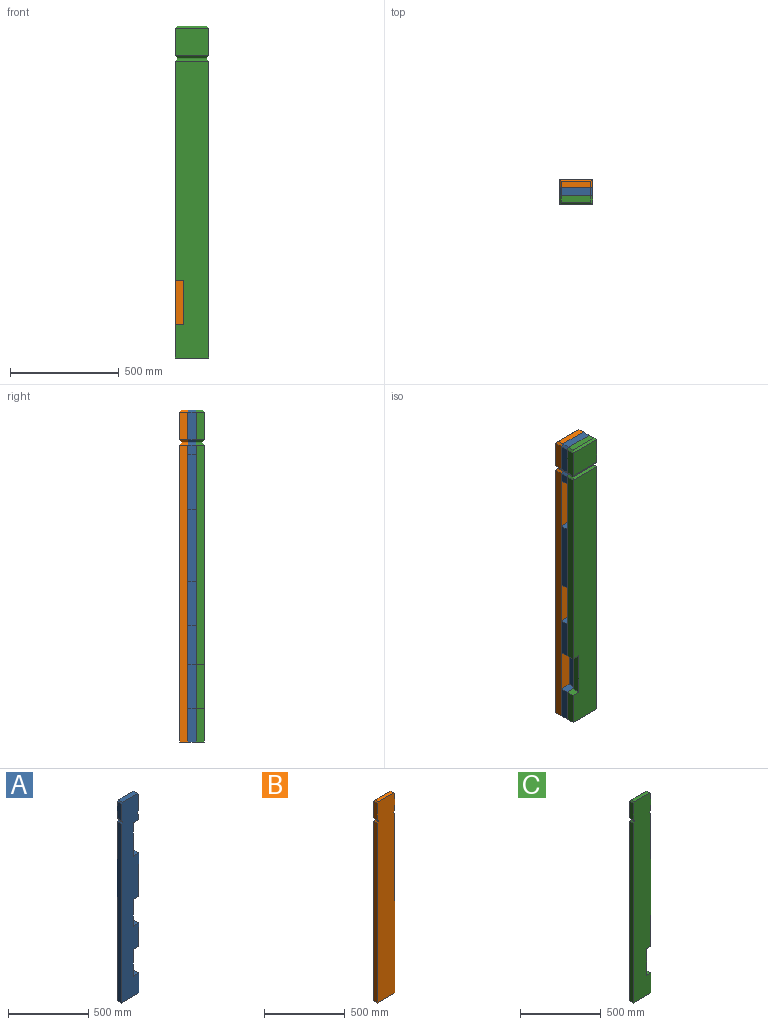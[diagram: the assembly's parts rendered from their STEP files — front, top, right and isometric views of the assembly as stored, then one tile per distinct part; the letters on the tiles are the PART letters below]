
ASSEMBLY  parts=3 mates=2
PART A: 28 faces, bbox 152.4x38.1x1524 mm
  f0: plane 177.8x38.1mm, normal (1,0,0), area 6774.2mm2, adj f4,f5,f13,f25
  f1: plane 127x38.1mm, normal (1,0,0), area 4838.7mm2, adj f4,f5,f20,f23
  f2: plane 127x38.1mm, normal (-1,0,0), area 4838.7mm2, adj f4,f5,f17,f24
  f3: plane 133.35x38.1mm, normal (0,0,1), area 5080.6mm2, adj f4,f5,f23,f24
  f4: plane 1524x152.4mm, normal (0,-1,0), area 198316.1mm2, adj f0,f1,f2,f3,f6,f7,f8,f9
  f5: plane 1524x152.4mm, normal (0,1,0), area 198316.1mm2, adj f0,f1,f2,f3,f6,f7,f8,f9
  f6: plane 41.28x38.1mm, normal (1,0,0), area 1572.6mm2, adj f4,f5,f14,f22
  f7: plane 330.2x38.1mm, normal (1,0,0), area 12580.6mm2, adj f4,f5,f11,f16
  f8: plane 1362.08x38.1mm, normal (-1,0,0), area 51895.1mm2, adj f4,f5,f9,f18
  f9: plane 152.4x38.1mm, normal (0,0,-1), area 5806.4mm2, adj f4,f5,f8,f10
  f10: plane 152.4x38.1mm, normal (1,0,0), area 5806.4mm2, adj f4,f5,f9,f27
  f11: plane 50.8x38.1mm, normal (0,0,-1), area 1935.5mm2, adj f4,f5,f7,f12
  f12: plane 203.2x38.1mm, normal (1,0,0), area 7741.9mm2, adj f4,f5,f11,f13
  f13: plane 50.8x38.1mm, normal (0,0,1), area 1935.5mm2, adj f0,f4,f5,f12
  f14: plane 50.8x38.1mm, normal (0,0,-1), area 1935.5mm2, adj f4,f5,f6,f15
  f15: plane 254x38.1mm, normal (1,0,0), area 9677.4mm2, adj f4,f5,f14,f16
  f16: plane 50.8x38.1mm, normal (0,0,1), area 1935.5mm2, adj f4,f5,f7,f15
  f17: plane 38.1x9.53mm, normal (-0.71,0,-0.71), area 513.2mm2, adj f2,f4,f5,f19
  f18: plane 38.1x9.53mm, normal (-0.71,0,0.71), area 513.2mm2, adj f4,f5,f8,f19
  f19: plane 38.1x6.35mm, normal (-1,0,0), area 241.9mm2, adj f4,f5,f17,f18
  f20: plane 38.1x9.53mm, normal (0.71,0,-0.71), area 513.2mm2, adj f1,f4,f5,f21
  f21: plane 38.1x6.35mm, normal (1,0,0), area 241.9mm2, adj f4,f5,f20,f22
  f22: plane 38.1x9.53mm, normal (0.71,0,0.71), area 513.2mm2, adj f4,f5,f6,f21
  f23: plane 38.1x9.53mm, normal (0.71,0,0.71), area 513.2mm2, adj f1,f3,f4,f5
  f24: plane 38.1x9.53mm, normal (-0.71,0,0.71), area 513.2mm2, adj f2,f3,f4,f5
  f25: plane 50.8x38.1mm, normal (0,0,-1), area 1935.5mm2, adj f0,f4,f5,f26
  f26: plane 203.2x38.1mm, normal (1,0,0), area 7741.9mm2, adj f4,f5,f25,f27
  f27: plane 50.8x38.1mm, normal (0,0,1), area 1935.5mm2, adj f4,f5,f10,f26
PART B: 21 faces, bbox 152.4x38.1x1524 mm
  f0: plane 152.4x127mm, normal (0,1,0), area 19354.8mm2, adj f3,f4,f17,f18
  f1: plane 38.1x9.53mm, normal (0.71,0,0.71), area 449.1mm2, adj f4,f5,f6,f17
  f2: plane 38.1x9.53mm, normal (-0.71,0,0.71), area 449.1mm2, adj f3,f5,f6,f17
  f3: plane 127x38.1mm, normal (-1,0,0), area 4838.7mm2, adj f0,f2,f6,f11
  f4: plane 127x38.1mm, normal (1,0,0), area 4838.7mm2, adj f0,f1,f6,f14
  f5: plane 133.35x28.58mm, normal (0,0,1), area 3810.5mm2, adj f1,f2,f6,f17
  f6: plane 1524x152.4mm, normal (0,-1,0), area 231864.5mm2, adj f1,f2,f3,f4,f5,f8,f9,f10
  f7: plane 1362.08x152.4mm, normal (0,1,0), area 207580.2mm2, adj f8,f9,f10,f20
  f8: plane 1362.08x38.1mm, normal (-1,0,0), area 51895.1mm2, adj f6,f7,f9,f12
  f9: plane 152.4x38.1mm, normal (0,0,-1), area 5806.4mm2, adj f6,f7,f8,f10
  f10: plane 1362.08x38.1mm, normal (1,0,0), area 51895.1mm2, adj f6,f7,f9,f16
  f11: plane 38.1x9.53mm, normal (-0.71,0,-0.71), area 449.1mm2, adj f3,f6,f13,f18
  f12: plane 38.1x9.53mm, normal (-0.71,0,0.71), area 449.1mm2, adj f6,f8,f13,f20
  f13: plane 28.58x6.35mm, normal (-1,0,0), area 181.5mm2, adj f6,f11,f12,f19
  f14: plane 38.1x9.53mm, normal (0.71,0,-0.71), area 449.1mm2, adj f4,f6,f15,f18
  f15: plane 28.58x6.35mm, normal (1,0,0), area 181.5mm2, adj f6,f14,f16,f19
  f16: plane 38.1x9.53mm, normal (0.71,0,0.71), area 449.1mm2, adj f6,f10,f15,f20
  f17: plane 152.4x9.53mm, normal (0,0.71,0.71), area 1924.6mm2, adj f0,f1,f2,f5
  f18: plane 152.4x9.53mm, normal (0,0.71,-0.71), area 1924.6mm2, adj f0,f11,f14,f19
  f19: plane 133.35x6.35mm, normal (0,1,0), area 846.8mm2, adj f13,f15,f18,f20
  f20: plane 152.4x9.53mm, normal (0,0.71,0.71), area 1924.6mm2, adj f7,f12,f16,f19
PART C: 25 faces, bbox 152.4x38.1x1524 mm
  f0: plane 152.4x127mm, normal (0,1,0), area 19354.8mm2, adj f4,f5,f21,f22
  f1: plane 38.1x9.53mm, normal (0.71,0,0.71), area 449.1mm2, adj f5,f6,f7,f21
  f2: plane 38.1x9.53mm, normal (-0.71,0,0.71), area 449.1mm2, adj f4,f6,f7,f21
  f3: plane 1006.48x38.1mm, normal (1,0,0), area 38346.7mm2, adj f7,f8,f17,f18
  f4: plane 127x38.1mm, normal (-1,0,0), area 4838.7mm2, adj f0,f2,f7,f12
  f5: plane 127x38.1mm, normal (1,0,0), area 4838.7mm2, adj f0,f1,f7,f15
  f6: plane 133.35x28.58mm, normal (0,0,1), area 3810.5mm2, adj f1,f2,f7,f21
  f7: plane 1524x152.4mm, normal (0,-1,0), area 224122.5mm2, adj f1,f2,f3,f4,f5,f6,f9,f10
  f8: plane 1362.08x152.4mm, normal (0,1,0), area 199838.3mm2, adj f3,f9,f10,f11,f18,f19,f20,f24
  f9: plane 1362.08x38.1mm, normal (-1,0,0), area 51895.1mm2, adj f7,f8,f10,f13
  f10: plane 152.4x38.1mm, normal (0,0,-1), area 5806.4mm2, adj f7,f8,f9,f11
  f11: plane 152.4x38.1mm, normal (1,0,0), area 5806.4mm2, adj f7,f8,f10,f20
  f12: plane 38.1x9.53mm, normal (-0.71,0,-0.71), area 449.1mm2, adj f4,f7,f14,f22
  f13: plane 38.1x9.53mm, normal (-0.71,0,0.71), area 449.1mm2, adj f7,f9,f14,f24
  f14: plane 28.58x6.35mm, normal (-1,0,0), area 181.5mm2, adj f7,f12,f13,f23
  f15: plane 38.1x9.53mm, normal (0.71,0,-0.71), area 449.1mm2, adj f5,f7,f16,f22
  f16: plane 28.58x6.35mm, normal (1,0,0), area 181.5mm2, adj f7,f15,f17,f23
  f17: plane 38.1x9.53mm, normal (0.71,0,0.71), area 449.1mm2, adj f3,f7,f16,f24
  f18: plane 38.1x38.1mm, normal (0,0,-1), area 1451.6mm2, adj f3,f7,f8,f19
  f19: plane 203.2x38.1mm, normal (1,0,0), area 7741.9mm2, adj f7,f8,f18,f20
  f20: plane 38.1x38.1mm, normal (0,0,1), area 1451.6mm2, adj f7,f8,f11,f19
  f21: plane 152.4x9.53mm, normal (0,0.71,0.71), area 1924.6mm2, adj f0,f1,f2,f6
  f22: plane 152.4x9.53mm, normal (0,0.71,-0.71), area 1924.6mm2, adj f0,f12,f15,f23
  f23: plane 133.35x6.35mm, normal (0,1,0), area 846.8mm2, adj f14,f16,f22,f24
  f24: plane 152.4x9.53mm, normal (0,0.71,0.71), area 1924.6mm2, adj f8,f13,f17,f23
PLACE A rot(axis=(0,0,1),180deg) t=(76.2,-57.15,0)mm
PLACE B t=(-76.2,19.05,0)mm
PLACE C rot(axis=(0,0,1),180deg) t=(76.2,-95.25,0)mm
MATE fastened B.f6 <-> A.f4  axis (0,-1,0) through (0,-19.05,0)mm
MATE fastened C.f7 <-> A.f5  axis (0,1,0) through (0,-57.15,0)mm
